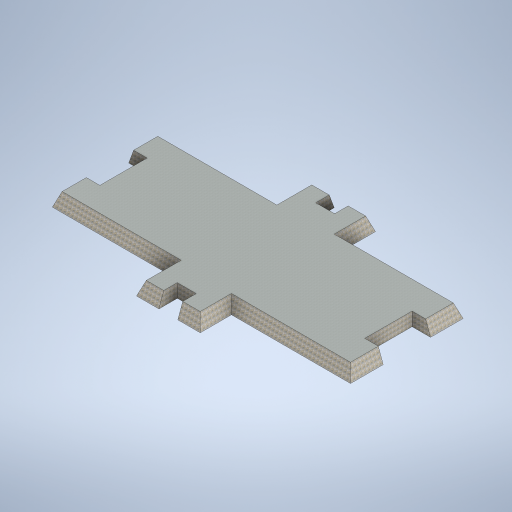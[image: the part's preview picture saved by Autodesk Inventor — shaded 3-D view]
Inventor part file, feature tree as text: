
AUTODESK INVENTOR PART (.ipt)
format: ipt  version: 2024.2 (Build 282272000, 272)  size: 363,008 bytes
history: native  units: mm
features: sketch x3, extrude x2
ambient origin geometry x8: Origin, YZ Plane, XZ Plane, XY Plane, X Axis, Y Axis, Z Axis, Center Point
bodies: Body1 (feature_tree)
feature tree (5):
  extrude  "Extrusion2"  Depth=3000.0mm
  extrude  "Extrusion3"  Depth=2000.0mm
  sketch  "Sketch3"  dims[d13=1400.0mm d14=2000.0mm d15=2800.0mm d16=1400.0mm d17=2000.0mm d18=2800.0mm d19=2000.0mm d21=3500.0mm d22=3500.0mm d23=2000.0mm d24=7000.0mm d25=2000.0mm d26=0.0mm d27=2000.0mm d28=7000.0mm d29=3500.0mm d30=3500.0mm d4=500.0mm d5=0.872665mm d6=500.0mm d7=0.872665mm]
  sketch  "Sketch1"  dims[d0=3000.0mm d1=3000.0mm]
  sketch  "Sketch2"  dims[d10=2000.0mm d11=3.490659mm d12=15200.0mm]
